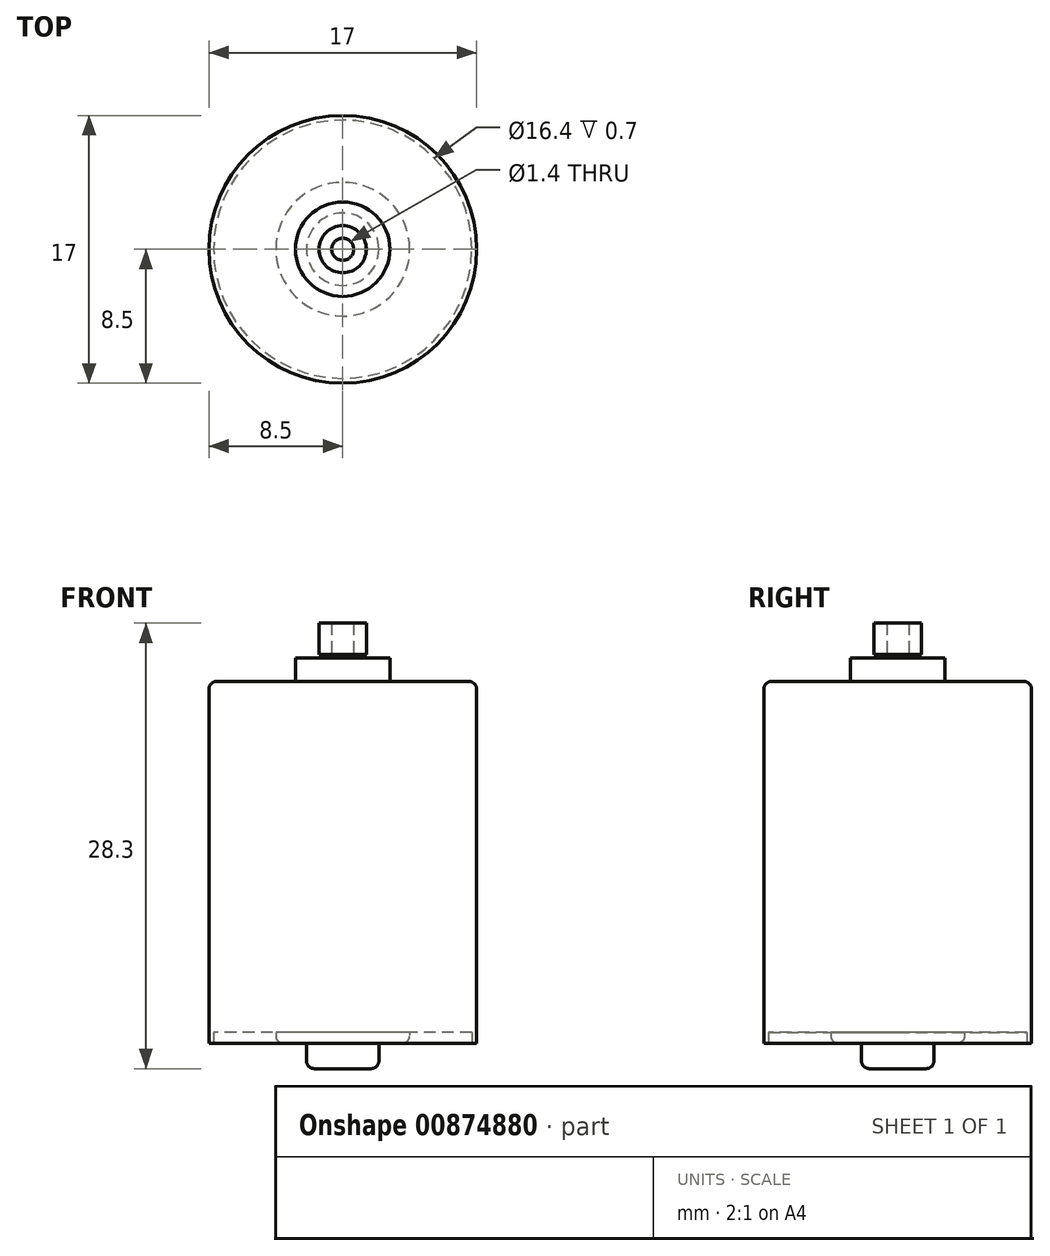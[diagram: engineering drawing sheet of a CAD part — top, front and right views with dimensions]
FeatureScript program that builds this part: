
annotation { "Feature Type Name" : "Feature", "Feature Type Description" : "" }
export const myFeature = defineFeature(function(context is Context, id is Id, definition is map)
    precondition{}
    {
        {
            var Q0;
            Q0=qCreatedBy(makeId("Top.planeOp"),FACE);
            var sketch = newSketch(context, id + "F0", { "sketchPlane" : qUnion([Q0])});
            skCircle(sketch, "E0", {"center": v(0, 0) * mm, "radius": 8.5 * mm});
            skCircle(sketch, "E1.0", {"center": v(0, 0) * mm, "radius": 8.2 * mm});
            skSolve(sketch);
        }
        {
            var Q0;
            Q0=makeQuery(id+"F0.imprint","IMPRINT",FACE,{"disambiguationData":[TD([[makeQuery(id+"F0.imprint","IMPRINT",EDGE,{"derivedFrom":sQuery(id+"F0.wireOp",EDGE,"E0")}),1.0]])]});
            var Q1;
            Q1=makeQuery(id+"F0.imprint","IMPRINT",FACE,{"disambiguationData":[TD([[makeQuery(id+"F0.imprint","IMPRINT",EDGE,{"derivedFrom":sQuery(id+"F0.wireOp",EDGE,"E1.0")}),1.0]])]});
            extrude(context, id + "F1", {"entities" : qUnion([Q0, Q1]), "depth" : 23 * mm, "offsetDistance" : 25 * mm});
        }
        {
            var Q0;
            Q0=makeQuery(id+"F0.imprint","IMPRINT",FACE,{"disambiguationData":[TD([[makeQuery(id+"F0.imprint","IMPRINT",EDGE,{"derivedFrom":sQuery(id+"F0.wireOp",EDGE,"E1.0")}),1.0]])]});
            extrude(context, id + "F2", {"entities" : qUnion([Q0]), "operationType" : NewBodyOperationType.REMOVE, "depth" : .7 * mm, "offsetDistance" : 25 * mm});
        }
        {
            var Q0;
            Q0=makeQuery(id+"F0.imprint","IMPRINT",FACE,{"disambiguationData":[TD([[makeQuery(id+"F0.imprint","IMPRINT",EDGE,{"derivedFrom":sQuery(id+"F0.wireOp",EDGE,"E1.0")}),1.0]])]});
            var sketch = newSketch(context, id + "F3", { "sketchPlane" : qUnion([Q0])});
            skCircle(sketch, "E2", {"center": v(0, 0) * mm, "radius": 4.25 * mm});
            skSolve(sketch);
        }
        {
            var Q0;
            Q0=makeQuery(id+"F3.imprint","IMPRINT",FACE,{"disambiguationData":[TD([[makeQuery(id+"F3.imprint","IMPRINT",EDGE,{"derivedFrom":sQuery(id+"F3.wireOp",EDGE,"E2")}),1.0]])]});
            extrude(context, id + "F4", {"entities" : qUnion([Q0]), "operationType" : NewBodyOperationType.ADD, "depth" : .7 * mm, "offsetDistance" : 25 * mm});
        }
        {
            var Q0;
            Q0=makeQuery(id+"F0.imprint","IMPRINT",FACE,{"disambiguationData":[TD([[makeQuery(id+"F0.imprint","IMPRINT",EDGE,{"derivedFrom":sQuery(id+"F0.wireOp",EDGE,"E1.0")}),1.0]])]});
            var sketch = newSketch(context, id + "F5", { "sketchPlane" : qUnion([Q0])});
            skCircle(sketch, "E3", {"center": v(0, 0) * mm, "radius": 2.3 * mm});
            skSolve(sketch);
        }
        {
            var Q0;
            Q0=makeQuery(id+"F5.imprint","IMPRINT",FACE,{"disambiguationData":[TD([[makeQuery(id+"F5.imprint","IMPRINT",EDGE,{"derivedFrom":sQuery(id+"F5.wireOp",EDGE,"E3")}),1.0]])]});
            extrude(context, id + "F6", {"entities" : qUnion([Q0]), "operationType" : NewBodyOperationType.ADD, "oppositeDirection" : true, "depth" : 1.6 * mm, "offsetDistance" : 25 * mm});
        }
        {
            var Q0;
            Q0=makeQuery(id+"F4.opExtrude","CAP_EDGE",EDGE,{"disambiguationData":[OSD([sQuery(id+"F3.wireOp",EDGE,"E2")])],"isStart":true});
            var Q1;
            Q1=makeQuery(id+"F6.opExtrude","CAP_EDGE",EDGE,{"disambiguationData":[OSD([sQuery(id+"F5.wireOp",EDGE,"E3")])],"isStart":false});
            var Q2;
            Q2=makeQuery(id+"F1.opExtrude","CAP_EDGE",EDGE,{"disambiguationData":[OSD([sQuery(id+"F0.wireOp",EDGE,"E0")])],"isStart":false});
            fillet(context, id + "F7", {"entities" : qUnion([Q0, Q1, Q2]), "radius" : .5 * mm, "tangentPropagation" : true, "allowEdgeOverflow" : false});
        }
        {
            var Q0;
            Q0=makeQuery(id+"F1.opExtrude","CAP_FACE",FACE,{"disambiguationData":[OSD([sQuery(id+"F0.wireOp",EDGE,"E0")])],"isStart":false});
            var sketch = newSketch(context, id + "F8", { "sketchPlane" : qUnion([Q0])});
            skCircle(sketch, "E4", {"center": v(0, 0) * mm, "radius": 3 * mm});
            skSolve(sketch);
        }
        {
            var Q0;
            Q0 = qSketchRegion(id + "F8", true);
            extrude(context, id + "F9", {"entities" : qUnion([Q0]), "operationType" : NewBodyOperationType.ADD, "depth" : 1.5 * mm, "offsetDistance" : 25 * mm});
        }
        {
            var Q0;
            Q0=makeQuery(id+"F9.opExtrude","CAP_FACE",FACE,{"disambiguationData":[OSD([sQuery(id+"F8.wireOp",EDGE,"E4")])],"isStart":false});
            var sketch = newSketch(context, id + "F10", { "sketchPlane" : qUnion([Q0])});
            skCircle(sketch, "E5", {"center": v(0, 0) * mm, "radius": 0.7 * mm});
            skSolve(sketch);
        }
        {
            var Q0;
            Q0=makeQuery(id+"F10.imprint","IMPRINT",FACE,{"disambiguationData":[TD([[makeQuery(id+"F10.imprint","IMPRINT",EDGE,{"derivedFrom":sQuery(id+"F10.wireOp",EDGE,"E5")}),1.0]])]});
            extrude(context, id + "F11", {"entities" : qUnion([Q0]), "operationType" : NewBodyOperationType.ADD, "depth" : 2.2 * mm, "offsetDistance" : 25 * mm});
        }
        {
            var Q0;
            Q0=makeQuery(id+"F11.opExtrude","CAP_FACE",FACE,{"disambiguationData":[OSD([sQuery(id+"F10.wireOp",EDGE,"E5")])],"isStart":false});
            var sketch = newSketch(context, id + "F12", { "sketchPlane" : qUnion([Q0])});
            skCircle(sketch, "E6", {"center": v(0, 0) * mm, "radius": 1.5 * mm});
            skSolve(sketch);
        }
        {
            var Q0;
            Q0=makeQuery(id+"F12.imprint","IMPRINT",FACE,{"disambiguationData":[TD([[makeQuery(id+"F12.imprint","IMPRINT",EDGE,{"derivedFrom":sQuery(id+"F12.wireOp",EDGE,"E6")}),1.0]])]});
            extrude(context, id + "F13", {"entities" : qUnion([Q0]), "oppositeDirection" : true, "depth" : 2 * mm, "offsetDistance" : 25 * mm});
        }
    });
